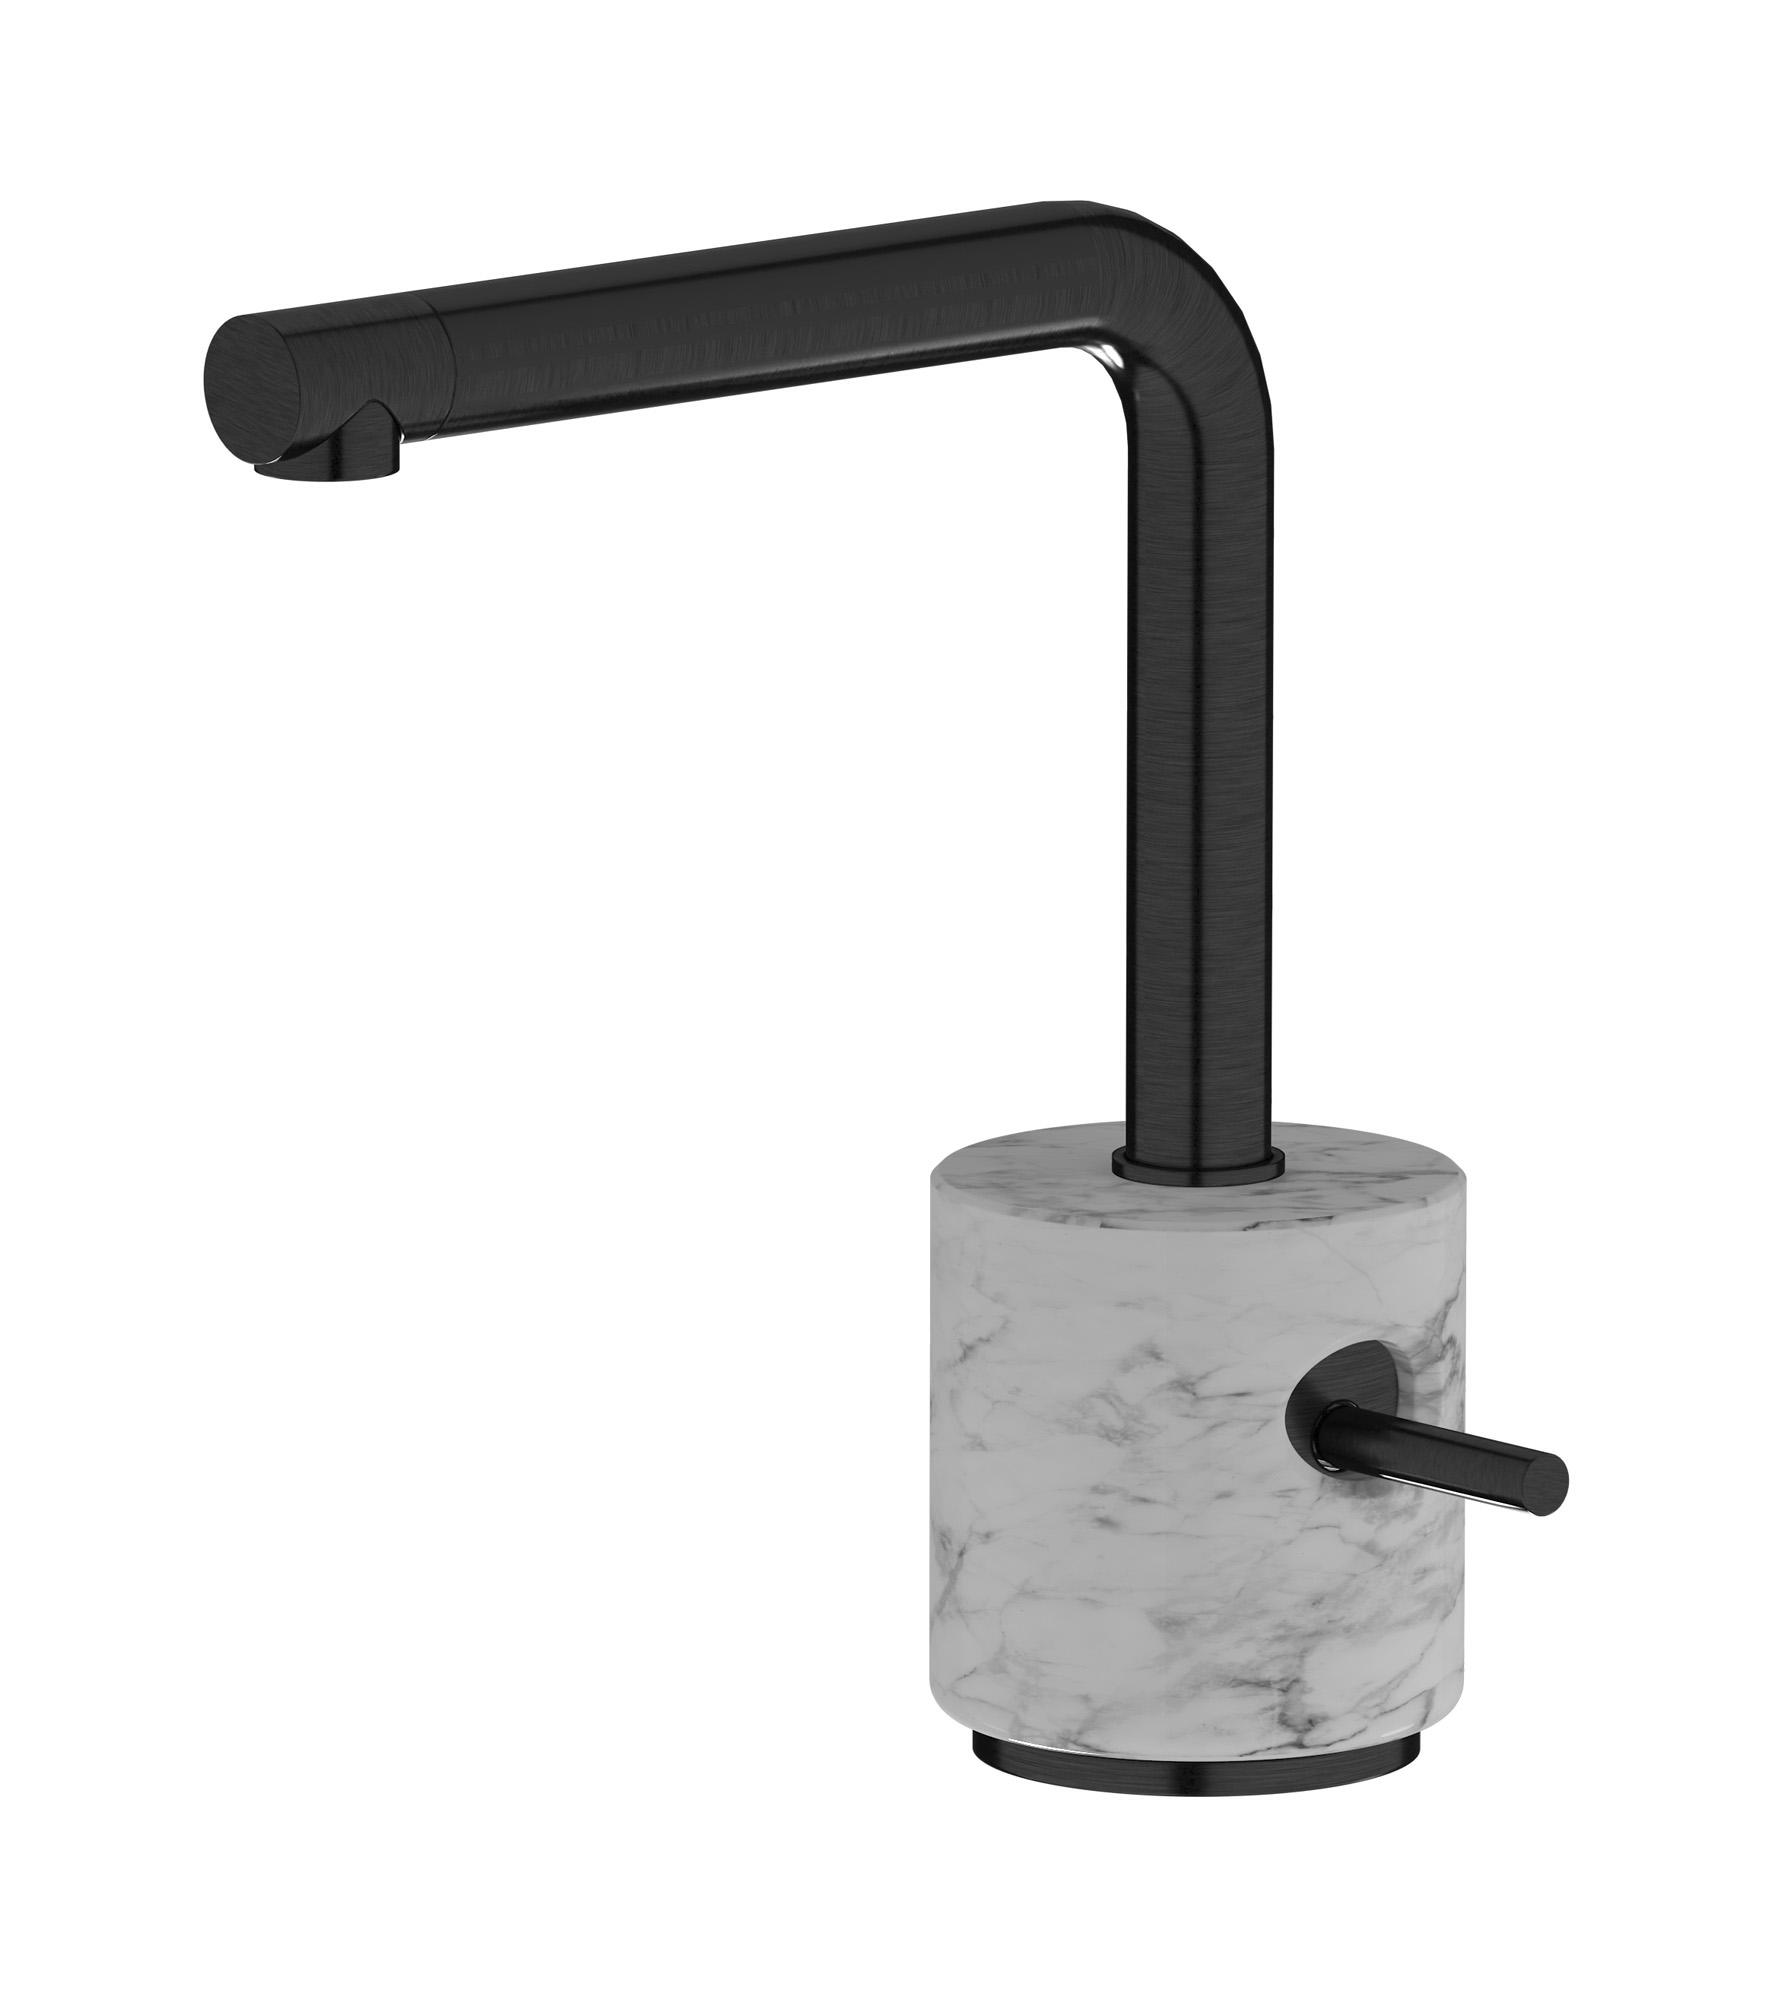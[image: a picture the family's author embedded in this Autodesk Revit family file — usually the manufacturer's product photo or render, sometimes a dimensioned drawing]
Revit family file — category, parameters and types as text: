
# Revit family: MM200_1
name_source: partatom
category: Apparecchi idraulici
units: mm (PartAtom-declared; Revit-internal decimal feet)

## family parameters
Basato su piano di lavoro = No
Condiviso = No
Mantieni orientamento annotazione = No
Numero OmniClass = 23.45.55.17
Punto di calcolo locali = No
Quota connettore circolare = Usa diametro
Sempre verticale = Sì
Taglio con vuoti quando caricato = No
Tipo di parte = Normale
Titolo OmniClass = Mixing Faucets

## types (14) — shared parameters
Cold water inlet = 10 mm  [stored 0.0328084 ft]
Commenti sul tipo = Washbasin mixer
Connessione CW = No
Connessione HW = No
Connessione di scarico = No
Connessione di ventilazione = No
Descrizione = Monohole washbasin mixer
Hot water inlet = 10 mm  [stored 0.0328084 ft]
Produttore = IB Rubinetterie S.p.A.
URL = https://www.weareib.it
zero-valued in all types: Prospetto di default

## per-type parameters (varying)
| type | Finishes surface | Immagine tipo | Modello |
| Chrome | IB_Chrome | MM200CC_1.jpg | MM200CC_1 |
| Platinum | IB_Platinum | MM200PL_1.jpg | MM200PL_1 |
| Brushed nickel | IB_Brushed nickel | MM200SS_1.jpg | MM200SS_1 |
| Natural brass | IB_Brass | MM200ON_1.jpg | MM200ON_1 |
| Matt white | IB_matt white | MM200BO_1.jpg | MM200BO_1 |
| Matt black | IB_matt black | MM200NP_1.jpg | MM200NP_1 |
| Black chrome | IB_Black chrome | MM200CF_1.jpg | MM200CF_1 |
| Brushed black chrome | IB_Brushed black chrome | MM200CS_1.jpg | MM200CS_1 |
| Pale gold | IB_Pale gold | MM200II_1.jpg | MM200II_1 |
| Brushed pale gold | IB_brushed pale gold | MM200IS_1.jpg | MM200IS_1 |
| Rose gold | IB_Rose gold | MM200RS_1.jpg | MM200RS_1 |
| Brushed rose gold | IB_Brushed rose gold | MM200SR_1.jpg | MM200SR_1 |
| Gold | IB_gold | MM200OO_1.jpg | MM200OO_1 |
| Brushed gold | IB_brushed gold | MM200OS_1.jpg | MM200OS_1 |

note: [stored X ft] marks values corroborated as IEEE doubles in the binary element streams (Revit-internal decimal feet)
